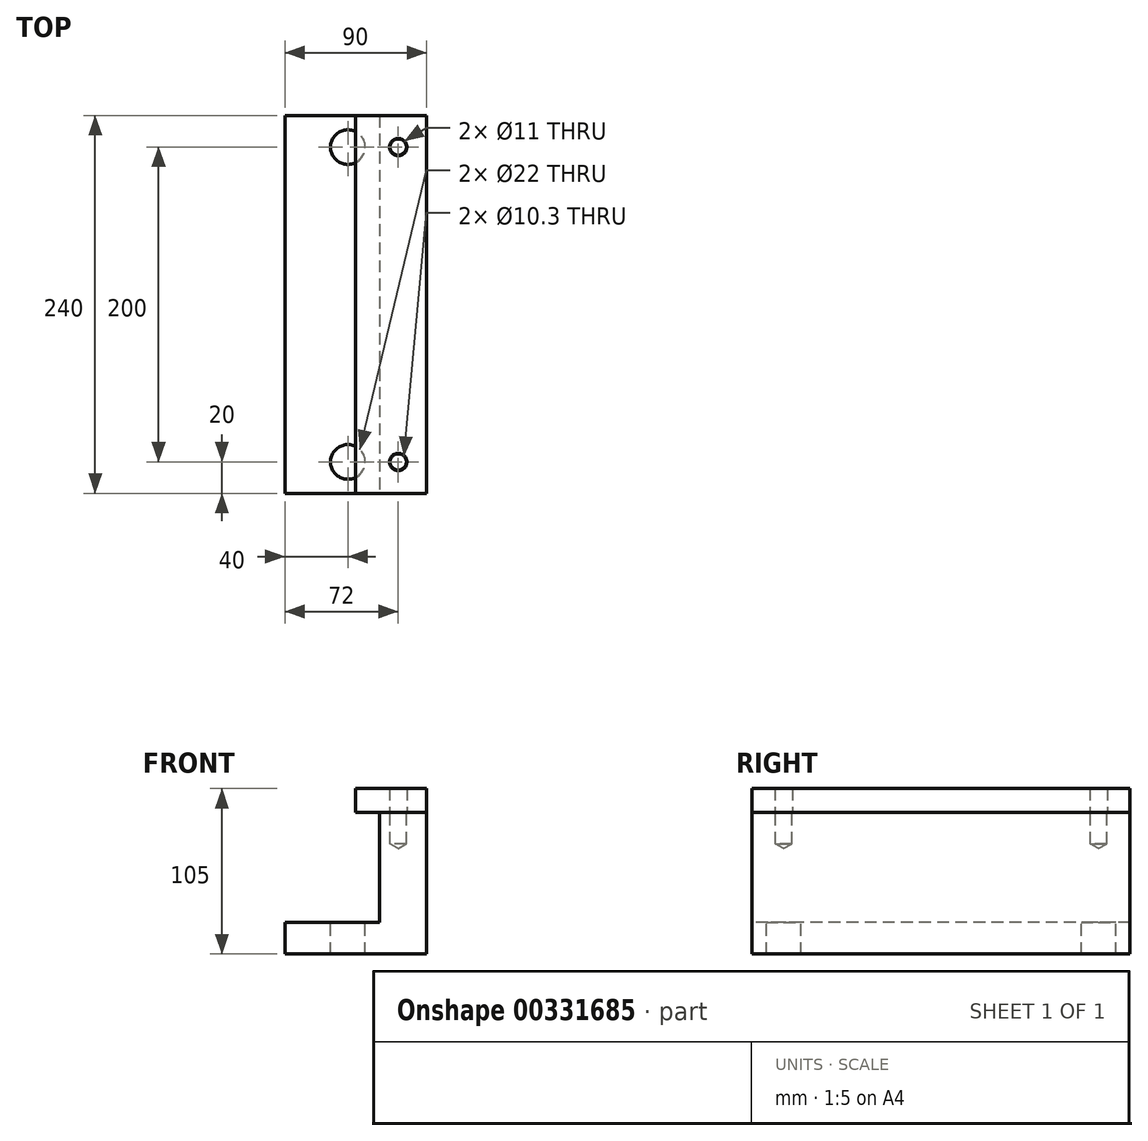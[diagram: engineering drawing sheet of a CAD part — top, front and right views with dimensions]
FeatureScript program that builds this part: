
annotation { "Feature Type Name" : "Feature", "Feature Type Description" : "" }
export const myFeature = defineFeature(function(context is Context, id is Id, definition is map)
    precondition{}
    {
        {
            var Q0;
            Q0=qCreatedBy(makeId("Front.planeOp"),FACE);
            var sketch = newSketch(context, id + "F0", { "sketchPlane" : qUnion([Q0])});
            skLineSegment(sketch, "E0.bottom", {"start": v(-90, 20) * mm, "end": v(-30, 20) * mm});
            skLineSegment(sketch, "E0.left", {"start": v(-90, 20) * mm, "end": v(-90, 0) * mm});
            skLineSegment(sketch, "E1", {"start": v(-30, 20) * mm, "end": v(-30, 90) * mm});
            skLineSegment(sketch, "E2", {"start": v(-30, 90) * mm, "end": v(0, 90) * mm});
            skLineSegment(sketch, "E3", {"start": v(-90, 0) * mm, "end": v(0, 0) * mm});
            skLineSegment(sketch, "E4", {"start": v(0, 90) * mm, "end": v(0, 0) * mm});
            skPoint(sketch, "E5", {"position": v(-60, 20) * mm});
            skSolve(sketch);
        }
        {
            var Q0;
            Q0=makeQuery(id+"F0.imprint","IMPRINT",FACE,{"disambiguationData":[TD([[makeQuery(id+"F0.imprint","IMPRINT",EDGE,{"derivedFrom":sQuery(id+"F0.wireOp",EDGE,"DewNuH0o-HxNw-LNmi-KTqx-rOA3MNoQVOCx.bottom")}),-1.0]])]});
            var Q1;
            Q1=makeQuery(id+"F0.imprint","IMPRINT",FACE,{"disambiguationData":[TD([[makeQuery(id+"F0.imprint","IMPRINT",EDGE,{"derivedFrom":sQuery(id+"F0.wireOp",EDGE,"E0.bottom")}),-1.0]])]});
            extrude(context, id + "F1", {"entities" : qUnion([Q0, Q1]), "oppositeDirection" : true, "depth" : 240 * mm});
        }
        {
            var Q0;
            Q0=makeQuery(id+"F1.opExtrude","SWEPT_FACE",FACE,{"disambiguationData":[OSD([sQuery(id+"F0.wireOp",EDGE,"E0.bottom")])]});
            var sketch = newSketch(context, id + "F2", { "sketchPlane" : qUnion([Q0])});
            skLineSegment(sketch, "E6.direction2", {"start": v(-50, 20) * mm, "end": v(-50, 220) * mm, "construction": true});
            skSolve(sketch);
        }
        {
            var Q0;
            Q0=sQuery(id+"F2.wireOp",VERTEX,"E6.direction2.end");
            var Q1;
            Q1=sQuery(id+"F2.wireOp",VERTEX,"E6.direction2.start");
            var Q2;
            Q2=sQuery(id+"F2.wireOp",VERTEX,"E6.direction2.end");
            var Q3;
            Q3=sQuery(id+"F2.wireOp",VERTEX,"E6.direction2.start");
            var Q4;
            Q4=makeQuery(id+"F1.opExtrude","SWEPT_BODY",BODY,{"disambiguationData":[OSD([sQuery(id+"F0.wireOp",EDGE,"E0.bottom"),sQuery(id+"F0.wireOp",EDGE,"E0.top"),sQuery(id+"F0.wireOp",EDGE,"E0.left"),sQuery(id+"F0.wireOp",EDGE,"E0.right"),sQuery(id+"F0.wireOp",EDGE,"DewNuH0o-HxNw-LNmi-KTqx-rOA3MNoQVOCx.bottom"),sQuery(id+"F0.wireOp",EDGE,"DewNuH0o-HxNw-LNmi-KTqx-rOA3MNoQVOCx.right"),sQuery(id+"F0.wireOp",EDGE,"64dFCOnm-yuBi-xCqR-AJ9k-m8Quuf6IYOCd")])]});
            hole(context, id + "F3", {"style" : HoleStyle.SIMPLE, "endStyle" : HoleEndStyle.THROUGH, "standardTappedOrClearance" : lookupTablePath({ "standard" : "ISO", "fit" : "Normal", "size" : "M20", "type" : "Clearance" }), "standardBlindInLast" : lookupTablePath({ "fit" : "Standard", "standard" : "ISO", "size" : "M20", "type" : "Clearance" }), "holeDiameter" : 22 * mm, "tappedDepth" : 12 * mm, "tapClearance" : 3, "locations" : qUnion([Q0, Q1, Q2, Q3]), "scope" : qUnion([Q4])});
        }
        {
            var Q0;
            Q0=makeQuery(id+"F1.opExtrude","SWEPT_FACE",FACE,{"disambiguationData":[OSD([sQuery(id+"F0.wireOp",EDGE,"E2")])]});
            var sketch = newSketch(context, id + "F4", { "sketchPlane" : qUnion([Q0])});
            skLineSegment(sketch, "E7", {"start": v(-18, 20) * mm, "end": v(-50, 20) * mm, "construction": true});
            skLineSegment(sketch, "E8", {"start": v(-18, 20) * mm, "end": v(-18, 220) * mm, "construction": true});
            skSolve(sketch);
        }
        {
            var Q0;
            Q0=sQuery(id+"F4.wireOp",VERTEX,"E8.end");
            var Q1;
            Q1=sQuery(id+"F4.wireOp",VERTEX,"E8.start");
            var Q2;
            Q2=makeQuery(id+"F1.opExtrude","SWEPT_BODY",BODY,{"disambiguationData":[OSD([sQuery(id+"F0.wireOp",EDGE,"E0.bottom"),sQuery(id+"F0.wireOp",EDGE,"E0.left"),sQuery(id+"F0.wireOp",EDGE,"E1"),sQuery(id+"F0.wireOp",EDGE,"NaaFn0YS-XE1H-n606-4f34-SzosIrA3H3QQ"),sQuery(id+"F0.wireOp",EDGE,"7f8gS3m4-UJ3g-k1Ge-VZki-832XXGclyYNS"),sQuery(id+"F0.wireOp",EDGE,"E2"),sQuery(id+"F0.wireOp",EDGE,"E3"),sQuery(id+"F0.wireOp",EDGE,"E4")])]});
            hole(context, id + "F5", {"style" : HoleStyle.SIMPLE, "endStyle" : HoleEndStyle.BLIND, "standardTappedOrClearance" : lookupTablePath({ "standard" : "ISO", "engagement" : "75%", "pitch" : "1.75 mm", "size" : "M12", "type" : "Tapped" }), "standardBlindInLast" : lookupTablePath({ "standard" : "ISO", "engagement" : "75%", "pitch" : "1.75 mm", "size" : "M12", "type" : "Tapped" }), "holeDiameter" : 10.3 * mm, "showTappedDepth" : true, "holeDepth" : 20 * mm, "tappedDepth" : 14.75 * mm, "tapClearance" : 3, "locations" : qUnion([Q0, Q1]), "scope" : qUnion([Q2]), "majorDiameter" : 12 * mm});
        }
        {
            var Q0;
            Q0=makeQuery(id+"F1.opExtrude","SWEPT_FACE",FACE,{"disambiguationData":[OSD([sQuery(id+"F0.wireOp",EDGE,"E2")])]});
            var sketch = newSketch(context, id + "F6", { "sketchPlane" : qUnion([Q0])});
            skLineSegment(sketch, "E9.bottom", {"start": v(0, 0) * mm, "end": v(-45, 0) * mm});
            skLineSegment(sketch, "E9.top", {"start": v(0, 240) * mm, "end": v(-45, 240) * mm});
            skLineSegment(sketch, "E9.left", {"start": v(0, 0) * mm, "end": v(0, 240) * mm});
            skLineSegment(sketch, "E9.right", {"start": v(-45, 0) * mm, "end": v(-45, 240) * mm});
            skSolve(sketch);
        }
        {
            var Q0;
            Q0 = qSketchRegion(id + "F6", true);
            extrude(context, id + "F7", {"entities" : qUnion([Q0]), "depth" : 15 * mm});
        }
        {
            var Q0;
            Q0=sQuery(id+"F4.wireOp",VERTEX,"E8.end");
            var Q1;
            Q1=sQuery(id+"F4.wireOp",VERTEX,"E8.start");
            var Q2;
            Q2=makeQuery(id+"F7.opExtrude","SWEPT_BODY",BODY,{"disambiguationData":[OSD([sQuery(id+"F6.wireOp",EDGE,"E9.bottom"),sQuery(id+"F6.wireOp",EDGE,"E9.top"),sQuery(id+"F6.wireOp",EDGE,"E9.left"),sQuery(id+"F6.wireOp",EDGE,"E9.right")])]});
            hole(context, id + "F8", {"style" : HoleStyle.SIMPLE, "endStyle" : HoleEndStyle.THROUGH, "oppositeDirection" : true, "standardTappedOrClearance" : lookupTablePath({ "standard" : "ISO", "fit" : "Normal", "size" : "M10", "type" : "Clearance" }), "standardBlindInLast" : lookupTablePath({ "fit" : "Standard", "standard" : "ISO", "size" : "M10", "type" : "Clearance" }), "holeDiameter" : 11 * mm, "tappedDepth" : 5.75 * mm, "tapClearance" : 3, "locations" : qUnion([Q0, Q1]), "scope" : qUnion([Q2])});
        }
    });
